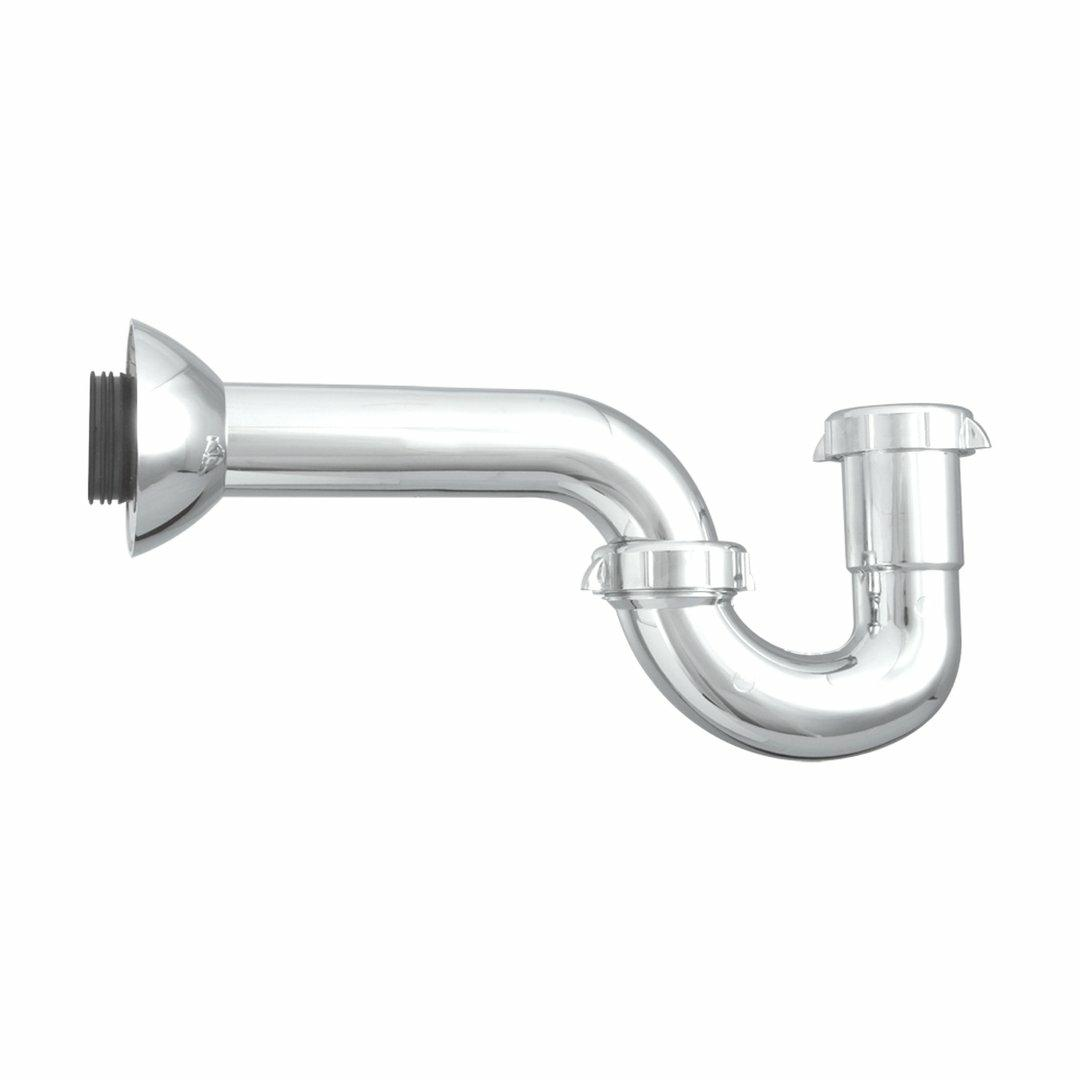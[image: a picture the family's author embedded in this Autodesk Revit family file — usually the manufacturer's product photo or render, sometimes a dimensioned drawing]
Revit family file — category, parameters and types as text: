
# Revit family: 01-4062-15 LAVAMANOS VESSEL HESTIA
name_source: partatom
category: Plumbing Fixtures
revit_build: Autodesk Revit 2018 (Build: 20170223_1515(x64)
units: mm (PartAtom-declared; Revit-internal decimal feet)

## family parameters
Cut with Voids When Loaded = No
Host = Face
OmniClass Number = 23.31.11.00
Part Type = Normal
Room Calculation Point = No
Round Connector Dimension = Use Diameter
Shared = No

## types (1)
- 01-4062-15
    Alto = 110 mm  [stored 0.360892 ft]
    Ancho = 420 mm
    CW Connection = Yes
    Ceramica = Porcelana
    Default Elevation = 0 mm  [stored 0 ft]
    Description = Lavamanos tipo vessel cuadrado
    HW Connection = Yes
    Largo = 420 mm
    Link Ficha Tecnica = http://infotecnica.gricol.com
    Manufacturer = Gricol
    Model = 01-4062-15
    Product Name = LAVAMANOS VESSEL GEB
    Push = push cromado
    Type Image = LAVAMANOS VESSEL HESTIA FOTO.jpg
    URL = https://www.gricol.com
    Vent Connection = No
    Waste Connection = No

note: [stored X ft] marks values corroborated as IEEE doubles in the binary element streams (Revit-internal decimal feet)

## geometry (parser evidence)
native form markers: Blend x8, Sweep x21
no freeform markers — native parametric forms only
